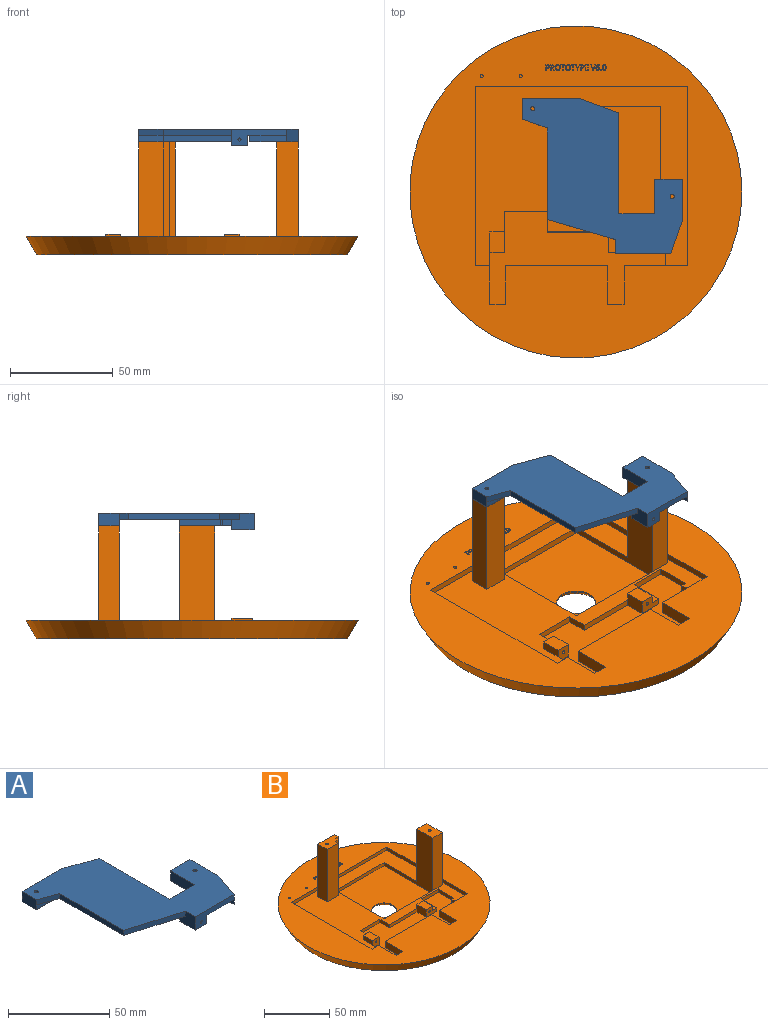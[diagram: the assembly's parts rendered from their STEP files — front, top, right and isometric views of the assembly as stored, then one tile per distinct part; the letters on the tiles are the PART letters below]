
ASSEMBLY  parts=2 mates=1
PART A: 32 faces, bbox 78x75.8x8 mm
  f0: plane 12x3mm, normal (0,-1,0), area 36mm2, adj f1,f5,f6,f20
  f1: plane 3x3mm, normal (1,0,0), area 9mm2, adj f0,f2,f6,f20
  f2: plane 35x3mm, normal (0,-1,0), area 105mm2, adj f1,f3,f6,f20
  f3: plane 19.23x7mm, normal (0.34,0.94,0), area 122.8mm2, adj f2,f4,f6,f21,f26
  f4: plane 27.77x6mm, normal (0,1,0), area 166.6mm2, adj f3,f5,f6,f26
  f5: plane 10x6mm, normal (-1,0,0), area 60mm2, adj f0,f4,f6,f22,f26
  f6: plane 47x10mm, normal (0,0,-1), area 294.5mm2, adj f0,f1,f2,f3,f4,f5,f31
  f7: plane 20x6mm, normal (1,0,0), area 120mm2, adj f8,f14,f15,f26
  f8: plane 13.5x6mm, normal (0,1,0), area 81mm2, adj f7,f9,f15,f26
  f9: plane 20x6mm, normal (-1,0,0), area 111mm2, adj f8,f10,f15,f20,f25,f26
  f10: plane 10.26x3mm, normal (0,1,0), area 30.8mm2, adj f9,f11,f15,f20
  f11: plane 3x1mm, normal (-1,0,0), area 3mm2, adj f10,f12,f15,f20
  f12: plane 18x3mm, normal (0,-1,0), area 54mm2, adj f11,f13,f15,f20
  f13: plane 15.5x3mm, normal (-1,0,0), area 46.5mm2, adj f12,f14,f15,f20
  f14: plane 16.5x6mm, normal (0.94,-0.33,0), area 104.9mm2, adj f7,f13,f15,f18,f26
  f15: plane 36.5x23.76mm, normal (0,0,-1), area 332.4mm2, adj f7,f8,f9,f10,f11,f12,f13,f14
  f16: plane 8x5mm, normal (0,1,0), area 40mm2, adj f17,f19,f20,f27
  f17: plane 11x8mm, normal (-1,0,0), area 76mm2, adj f16,f18,f20,f24,f26,f27
  f18: plane 27x8mm, normal (0,-1,0), area 119.2mm2, adj f14,f17,f19,f20,f26,f27,f28
  f19: plane 11x5mm, normal (1,0,0), area 55mm2, adj f16,f18,f20,f27
  f20: plane 72.24x68.8mm, normal (0,0,-1), area 2401.6mm2, adj f0,f1,f2,f9,f10,f11,f12,f13
  f21: plane 49.3x3mm, normal (1,0,0), area 147.9mm2, adj f3,f20,f25,f26
  f22: plane 12x4.37mm, normal (-0.34,-0.94,0), area 38.3mm2, adj f5,f20,f23,f26
  f23: plane 44.63x3mm, normal (-1,0,0), area 133.9mm2, adj f20,f22,f24,f26
  f24: plane 33.24x9.8mm, normal (-0.28,-0.96,0), area 104mm2, adj f17,f20,f23,f26
  f25: plane 17.5x3mm, normal (0,1,0), area 52.5mm2, adj f9,f20,f21,f26
  f26: plane 78x75.8mm, normal (0,0,1), area 3116.5mm2, adj f3,f4,f5,f7,f8,f9,f14,f17
  f27: plane 11x8mm, normal (0,0,-1), area 88mm2, adj f16,f17,f18,f19
  f28: cylinder r=0.75mm len=5mm, axis (0,-1,0), area 23.6mm2, adj f18,f29
  f29: plane 1.5x1.5mm, normal (0,-1,0), area 1.8mm2, adj f28
  f30: cylinder r=1mm len=6mm, axis (0,0,1), area 37.7mm2, adj f15,f26
  f31: cylinder r=1mm len=6mm, axis (0,0,1), area 37.7mm2, adj f6,f26
PART B: 260 faces, bbox 162x162x55 mm
  f0: plane 103.4x87.4mm, normal (0,0,1), area 4227.3mm2, adj f5,f6,f7,f8,f9,f16,f18,f19
  f1: plane 162x162mm, normal (0,0,1), area 11243.2mm2, adj f9,f10,f11,f12,f13,f14,f15,f16
  f2: plane 52.5x52.5mm, normal (0,0,1), area 2472.7mm2, adj f3,f24,f25,f26,f28
  f3: cylinder r=9.5mm len=19mm, axis (0,0,1), area 36.8mm2, adj f2,f41
  f4: plane 151.61x151.61mm, normal (0,0,-1), area 17636.8mm2, adj f40,f41
  f5: plane 18.5x3mm, normal (0,-1,0), area 55.5mm2, adj f0,f6,f27,f29
  f6: plane 17x3mm, normal (-1,0,0), area 51mm2, adj f0,f5,f7,f29
  f7: plane 3x2.5mm, normal (0,1,0), area 7.5mm2, adj f0,f6,f8,f29
  f8: plane 6.4x3mm, normal (-1,0,0), area 19.2mm2, adj f0,f7,f9,f29
  f9: plane 31x6mm, normal (0,1,0), area 153mm2, adj f0,f1,f8,f10,f29,f33
  f10: plane 19x6mm, normal (-1,0,0), area 114mm2, adj f1,f9,f11,f29
  f11: plane 8x6mm, normal (0,1,0), area 48mm2, adj f1,f10,f12,f29
  f12: plane 19x6mm, normal (1,0,0), area 114mm2, adj f1,f11,f13,f29
  f13: plane 50x6mm, normal (0,1,0), area 300mm2, adj f1,f12,f14,f29
  f14: plane 19x6mm, normal (-1,0,0), area 114mm2, adj f1,f13,f15,f29
  f15: plane 7.4x6mm, normal (0,1,0), area 44.4mm2, adj f1,f14,f16,f29
  f16: plane 25.4x6mm, normal (1,0,0), area 133.2mm2, adj f0,f1,f15,f17,f29,f30
  f17: plane 7x7mm, normal (0,-1,0), area 47.2mm2, adj f16,f18,f29,f35,f36,f44
  f18: plane 20x7mm, normal (1,0,0), area 100mm2, adj f0,f17,f19,f29,f34,f36
  f19: plane 21x3mm, normal (0,-1,0), area 63mm2, adj f0,f18,f20,f29
  f20: plane 10x3mm, normal (-1,0,0), area 30mm2, adj f0,f19,f21,f29
  f21: plane 29.9x3mm, normal (0,-1,0), area 89.7mm2, adj f0,f20,f22,f29
  f22: plane 10x7mm, normal (-1,0,0), area 70mm2, adj f21,f23,f29,f37,f39
  f23: plane 11.5x7mm, normal (0,-1,0), area 60.7mm2, adj f0,f22,f27,f29,f38,f39,f42
  f24: plane 52.5x52mm, normal (1,0,0), area 304.5mm2, adj f0,f2,f25,f28,f246,f251
  f25: plane 52.5x52mm, normal (0,-1,0), area 304.5mm2, adj f0,f2,f24,f26,f247,f251
  f26: plane 52.5x52mm, normal (-1,0,0), area 1000.3mm2, adj f0,f2,f25,f28,f253,f254,f255
  f27: plane 17x3mm, normal (1,0,0), area 51mm2, adj f0,f5,f23,f29
  f28: plane 52.5x3mm, normal (0,1,0), area 157.5mm2, adj f0,f2,f24,f26
  f29: plane 87.9x45.4mm, normal (0,0,1), area 1872.7mm2, adj f5,f6,f7,f8,f9,f10,f11,f12
  f30: plane 7x3mm, normal (0,1,0), area 21mm2, adj f0,f1,f16,f31
  f31: plane 87.4x3mm, normal (1,0,0), area 262.2mm2, adj f0,f1,f30,f32
  f32: plane 103.4x3mm, normal (0,-1,0), area 310.2mm2, adj f0,f1,f31,f33
  f33: plane 87.4x3mm, normal (-1,0,0), area 262.2mm2, adj f0,f1,f9,f32
  f34: plane 7x4mm, normal (0,1,0), area 28mm2, adj f0,f18,f35,f36
  f35: plane 10x4mm, normal (-1,0,0), area 40mm2, adj f0,f17,f34,f36
  f36: plane 10x7mm, normal (0,0,1), area 70mm2, adj f17,f18,f34,f35
  f37: plane 7x4mm, normal (0,1,0), area 28mm2, adj f0,f22,f38,f39
  f38: plane 10x4mm, normal (1,0,0), area 40mm2, adj f0,f23,f37,f39
  f39: plane 10x7mm, normal (0,0,1), area 70mm2, adj f22,f23,f37,f38
  f40: cone r=81mm half-angle=30deg, axis (0,0,1), area 5119.4mm2, adj f1,f4
  f41: cone r=11.5mm half-angle=40deg, axis (0,0,-1), area 205.3mm2, adj f3,f4
  f42: cylinder r=0.75mm len=5mm, axis (0,-1,0), area 23.6mm2, adj f23,f43
  f43: plane 1.5x1.5mm, normal (0,-1,0), area 1.8mm2, adj f42
  f44: cylinder r=0.75mm len=5mm, axis (0,-1,0), area 23.6mm2, adj f17,f45
  f45: plane 1.5x1.5mm, normal (0,-1,0), area 1.8mm2, adj f44
  f46: cylinder r=0.75mm len=3mm, axis (0,0,1), area 14.1mm2, adj f1,f47
  f47: plane 1.5x1.5mm, normal (0,0,1), area 1.8mm2, adj f46
  f48: cylinder r=0.75mm len=3mm, axis (0,0,1), area 14.1mm2, adj f1,f49
  f49: plane 1.5x1.5mm, normal (0,0,1), area 1.8mm2, adj f48
  f50: plane 0.5x0.32mm, normal (0,1,0), area 0.2mm2, adj f1,f51,f57,f58
  f51: plane 2.44x0.5mm, normal (-1,0,0), area 1.2mm2, adj f1,f50,f52,f58
  f52: plane 0.86x0.5mm, normal (0,1,0), area 0.4mm2, adj f1,f51,f53,f58
  f53: plane 0.5x0.28mm, normal (-1,0,0), area 0.1mm2, adj f1,f52,f54,f58
  f54: plane 2.04x0.5mm, normal (0,-1,0), area 1mm2, adj f1,f53,f55,f58
  f55: plane 0.5x0.28mm, normal (1,0,0), area 0.1mm2, adj f1,f54,f56,f58
  f56: plane 0.86x0.5mm, normal (0,1,0), area 0.4mm2, adj f1,f55,f57,f58
  f57: plane 2.44x0.5mm, normal (1,0,0), area 1.2mm2, adj f1,f50,f56,f58
  f58: plane 2.72x2.04mm, normal (0,0,1), area 1.3mm2, adj f50,f51,f52,f53,f54,f55,f56,f57
  f59: extruded ~0.86x0.5mm, area 0.4mm2, adj f60,f74,f75,f238
  f60: extruded ~0.86x0.5mm, area 0.4mm2, adj f59,f61,f75,f238
  f61: extruded ~0.5x0.44mm, area 0.3mm2, adj f60,f62,f75,f238
  f62: extruded ~0.5x0.45mm, area 0.3mm2, adj f61,f63,f75,f238
  f63: extruded ~0.86x0.5mm, area 0.4mm2, adj f62,f64,f75,f238
  f64: extruded ~0.86x0.5mm, area 0.4mm2, adj f63,f65,f75,f238
  f65: extruded ~0.5x0.45mm, area 0.3mm2, adj f64,f74,f75,f238
  f66: extruded ~1.05x0.5mm, area 0.5mm2, adj f1,f67,f73,f75
  f67: extruded ~1.04x0.5mm, area 0.5mm2, adj f1,f66,f68,f75
  f68: extruded ~0.67x0.5mm, area 0.4mm2, adj f1,f67,f69,f75
  f69: extruded ~0.67x0.5mm, area 0.4mm2, adj f1,f68,f70,f75
  f70: extruded ~1.05x0.5mm, area 0.5mm2, adj f1,f69,f71,f75
  f71: extruded ~1.04x0.5mm, area 0.5mm2, adj f1,f70,f72,f75
  f72: extruded ~0.67x0.5mm, area 0.4mm2, adj f1,f71,f73,f75
  f73: extruded ~0.68x0.5mm, area 0.4mm2, adj f1,f66,f72,f75
  f74: extruded ~0.5x0.44mm, area 0.3mm2, adj f59,f65,f75,f238
  f75: plane 2.8x1.8mm, normal (0,0,1), area 1.9mm2, adj f59,f60,f61,f62,f63,f64,f65,f66
  f76: extruded ~0.5x0.41mm, area 0.2mm2, adj f77,f100,f101,f239
  f77: extruded ~0.5x0.31mm, area 0.2mm2, adj f76,f78,f101,f239
  f78: extruded ~0.5x0.26mm, area 0.2mm2, adj f77,f79,f101,f239
  f79: extruded ~0.5x0.36mm, area 0.2mm2, adj f78,f80,f101,f239
  f80: extruded ~0.5x0.25mm, area 0.1mm2, adj f79,f81,f101,f239
  f81: extruded ~0.5x0.22mm, area 0.1mm2, adj f80,f82,f101,f239
  f82: extruded ~0.5x0.31mm, area 0.2mm2, adj f81,f83,f101,f239
  f83: extruded ~0.5x0.41mm, area 0.2mm2, adj f82,f84,f101,f239
  f84: extruded ~0.5x0.42mm, area 0.2mm2, adj f83,f100,f101,f239
  f85: extruded ~1.2x0.5mm, area 0.6mm2, adj f1,f86,f99,f101
  f86: extruded ~0.88x0.5mm, area 0.5mm2, adj f1,f85,f87,f101
  f87: extruded ~0.67x0.5mm, area 0.4mm2, adj f1,f86,f88,f101
  f88: extruded ~0.63x0.5mm, area 0.3mm2, adj f1,f87,f89,f101
  f89: extruded ~0.67x0.5mm, area 0.4mm2, adj f1,f88,f90,f101
  f90: extruded ~0.6x0.5mm, area 0.3mm2, adj f1,f89,f91,f101
  f91: extruded ~0.58x0.5mm, area 0.3mm2, adj f1,f90,f92,f101
  f92: extruded ~0.65x0.5mm, area 0.4mm2, adj f1,f91,f93,f101
  f93: plane 0.5x0.02mm, normal (0,-1,0), area 0mm2, adj f1,f92,f94,f101
  f94: extruded ~0.86x0.5mm, area 0.5mm2, adj f1,f93,f95,f101
  f95: extruded ~0.67x0.5mm, area 0.4mm2, adj f1,f94,f96,f101
  f96: extruded ~0.5x0.33mm, area 0.2mm2, adj f1,f95,f97,f101
  f97: plane 0.5x0.27mm, normal (-1,0,0), area 0.1mm2, adj f1,f96,f98,f101
  f98: extruded ~0.5x0.33mm, area 0.2mm2, adj f1,f97,f99,f101
  f99: extruded ~0.92x0.5mm, area 0.5mm2, adj f1,f85,f98,f101
  f100: extruded ~0.5x0.48mm, area 0.3mm2, adj f76,f84,f101,f239
  f101: plane 2.79x1.77mm, normal (0,0,1), area 1.9mm2, adj f76,f77,f78,f79,f80,f81,f82,f83
  f102: plane 0.5x0.29mm, normal (0,-1,0), area 0.1mm2, adj f103,f116,f117,f240
  f103: plane 1.1x0.5mm, normal (-1,0,0), area 0.6mm2, adj f102,f104,f117,f240
  f104: plane 0.5x0.35mm, normal (0,1,0), area 0.2mm2, adj f103,f105,f117,f240
  f105: extruded ~0.55x0.5mm, area 0.3mm2, adj f104,f106,f117,f240
  f106: extruded ~0.5x0.4mm, area 0.2mm2, adj f105,f107,f117,f240
  f107: extruded ~0.5x0.44mm, area 0.2mm2, adj f106,f116,f117,f240
  f108: extruded ~0.64x0.5mm, area 0.4mm2, adj f1,f109,f115,f117
  f109: extruded ~1.02x0.79mm, area 0.7mm2, adj f1,f108,f110,f117
  f110: plane 0.7x0.5mm, normal (0,-1,0), area 0.4mm2, adj f1,f109,f111,f117
  f111: plane 2.72x0.5mm, normal (1,0,0), area 1.4mm2, adj f1,f110,f112,f117
  f112: plane 0.5x0.32mm, normal (0,1,0), area 0.2mm2, adj f1,f111,f113,f117
  f113: plane 1.07x0.5mm, normal (-1,0,0), area 0.5mm2, adj f1,f112,f114,f117
  f114: plane 0.5x0.32mm, normal (0,1,0), area 0.2mm2, adj f1,f113,f115,f117
  f115: extruded ~0.81x0.5mm, area 0.4mm2, adj f1,f108,f114,f117
  f116: extruded ~0.61x0.5mm, area 0.3mm2, adj f102,f107,f117,f240
  f117: plane 2.72x1.72mm, normal (0,0,1), area 1.8mm2, adj f102,f103,f104,f105,f106,f107,f108,f109
  f118: extruded ~0.84x0.5mm, area 0.4mm2, adj f119,f133,f134,f241
  f119: extruded ~0.83x0.5mm, area 0.4mm2, adj f118,f120,f134,f241
  f120: extruded ~0.69x0.5mm, area 0.4mm2, adj f119,f121,f134,f241
  f121: extruded ~0.68x0.5mm, area 0.4mm2, adj f120,f122,f134,f241
  f122: extruded ~0.83x0.5mm, area 0.4mm2, adj f121,f123,f134,f241
  f123: extruded ~0.84x0.5mm, area 0.4mm2, adj f122,f124,f134,f241
  f124: extruded ~0.68x0.5mm, area 0.4mm2, adj f123,f133,f134,f241
  f125: extruded ~1.03x0.5mm, area 0.6mm2, adj f1,f126,f132,f134
  f126: extruded ~1.03x0.5mm, area 0.6mm2, adj f1,f125,f127,f134
  f127: extruded ~0.91x0.5mm, area 0.5mm2, adj f1,f126,f128,f134
  f128: extruded ~0.93x0.5mm, area 0.5mm2, adj f1,f127,f129,f134
  f129: extruded ~1.03x0.5mm, area 0.6mm2, adj f1,f128,f130,f134
  f130: extruded ~1.04x0.5mm, area 0.6mm2, adj f1,f129,f131,f134
  f131: extruded ~0.93x0.5mm, area 0.5mm2, adj f1,f130,f132,f134
  f132: extruded ~0.92x0.5mm, area 0.5mm2, adj f1,f125,f131,f134
  f133: extruded ~0.68x0.5mm, area 0.4mm2, adj f118,f124,f134,f241
  f134: plane 2.8x2.5mm, normal (0,0,1), area 2.3mm2, adj f118,f119,f120,f121,f122,f123,f124,f125
  f135: plane 0.5x0.32mm, normal (0,1,0), area 0.2mm2, adj f1,f136,f142,f143
  f136: plane 2.44x0.5mm, normal (-1,0,0), area 1.2mm2, adj f1,f135,f137,f143
  f137: plane 0.86x0.5mm, normal (0,1,0), area 0.4mm2, adj f1,f136,f138,f143
  f138: plane 0.5x0.28mm, normal (-1,0,0), area 0.1mm2, adj f1,f137,f139,f143
  f139: plane 2.04x0.5mm, normal (0,-1,0), area 1mm2, adj f1,f138,f140,f143
  f140: plane 0.5x0.28mm, normal (1,0,0), area 0.1mm2, adj f1,f139,f141,f143
  f141: plane 0.86x0.5mm, normal (0,1,0), area 0.4mm2, adj f1,f140,f142,f143
  f142: plane 2.44x0.5mm, normal (1,0,0), area 1.2mm2, adj f1,f135,f141,f143
  f143: plane 2.72x2.04mm, normal (0,0,1), area 1.3mm2, adj f135,f136,f137,f138,f139,f140,f141,f142
  f144: plane 1.36x0.72mm, normal (0.88,-0.47,0), area 0.8mm2, adj f1,f145,f152,f153
  f145: plane 1.36x0.72mm, normal (-0.88,-0.47,0), area 0.8mm2, adj f1,f144,f146,f153
  f146: plane 0.5x0.35mm, normal (0,-1,0), area 0.2mm2, adj f1,f145,f147,f153
  f147: plane 1.68x0.91mm, normal (0.88,0.47,0), area 1mm2, adj f1,f146,f148,f153
  f148: plane 1.04x0.5mm, normal (1,0,0), area 0.5mm2, adj f1,f147,f149,f153
  f149: plane 0.5x0.32mm, normal (0,1,0), area 0.2mm2, adj f1,f148,f150,f153
  f150: plane 1.05x0.5mm, normal (-1,0,0), area 0.5mm2, adj f1,f149,f151,f153
  f151: plane 1.66x0.91mm, normal (-0.88,0.48,0), area 0.9mm2, adj f1,f150,f152,f153
  f152: plane 0.5x0.34mm, normal (0,-1,0), area 0.2mm2, adj f1,f144,f151,f153
  f153: plane 2.72x2.13mm, normal (0,0,1), area 1.4mm2, adj f144,f145,f146,f147,f148,f149,f150,f151
  f154: plane 1.51x0.5mm, normal (0,1,0), area 0.8mm2, adj f1,f155,f165,f166
  f155: plane 0.5x0.28mm, normal (-1,0,0), area 0.1mm2, adj f1,f154,f156,f166
  f156: plane 1.2x0.5mm, normal (0,-1,0), area 0.6mm2, adj f1,f155,f157,f166
  f157: plane 1x0.5mm, normal (-1,0,0), area 0.5mm2, adj f1,f156,f158,f166
  f158: plane 1.13x0.5mm, normal (0,1,0), area 0.6mm2, adj f1,f157,f159,f166
  f159: plane 0.5x0.28mm, normal (-1,0,0), area 0.1mm2, adj f1,f158,f160,f166
  f160: plane 1.13x0.5mm, normal (0,-1,0), area 0.6mm2, adj f1,f159,f161,f166
  f161: plane 0.88x0.5mm, normal (-1,0,0), area 0.4mm2, adj f1,f160,f162,f166
  f162: plane 1.2x0.5mm, normal (0,1,0), area 0.6mm2, adj f1,f161,f163,f166
  f163: plane 0.5x0.28mm, normal (-1,0,0), area 0.1mm2, adj f1,f162,f164,f166
  f164: plane 1.51x0.5mm, normal (0,-1,0), area 0.8mm2, adj f1,f163,f165,f166
  f165: plane 2.72x0.5mm, normal (1,0,0), area 1.4mm2, adj f1,f154,f164,f166
  f166: plane 2.72x1.51mm, normal (0,0,1), area 1.8mm2, adj f154,f155,f156,f157,f158,f159,f160,f161
  f167: plane 0.5x0.34mm, normal (0,-1,0), area 0.2mm2, adj f1,f168,f175,f176
  f168: plane 1.75x0.62mm, normal (0.94,-0.33,0), area 0.9mm2, adj f1,f167,f169,f176
  f169: extruded ~0.6x0.5mm, area 0.3mm2, adj f1,f168,f170,f176
  f170: extruded ~0.59x0.5mm, area 0.3mm2, adj f1,f169,f171,f176
  f171: plane 1.76x0.62mm, normal (-0.94,-0.33,0), area 0.9mm2, adj f1,f170,f172,f176
  f172: plane 0.5x0.34mm, normal (0,-1,0), area 0.2mm2, adj f1,f171,f173,f176
  f173: plane 2.72x0.97mm, normal (0.94,0.34,0), area 1.4mm2, adj f1,f172,f174,f176
  f174: plane 0.5x0.31mm, normal (0,1,0), area 0.2mm2, adj f1,f173,f175,f176
  f175: plane 2.72x0.98mm, normal (-0.94,0.34,0), area 1.4mm2, adj f1,f167,f174,f176
  f176: plane 2.72x2.27mm, normal (0,0,1), area 1.7mm2, adj f167,f168,f169,f170,f171,f172,f173,f174
  f177: extruded ~0.84x0.5mm, area 0.4mm2, adj f178,f192,f193,f242
  f178: extruded ~0.83x0.5mm, area 0.4mm2, adj f177,f179,f193,f242
  f179: extruded ~0.69x0.5mm, area 0.4mm2, adj f178,f180,f193,f242
  f180: extruded ~0.68x0.5mm, area 0.4mm2, adj f179,f181,f193,f242
  f181: extruded ~0.83x0.5mm, area 0.4mm2, adj f180,f182,f193,f242
  f182: extruded ~0.84x0.5mm, area 0.4mm2, adj f181,f183,f193,f242
  f183: extruded ~0.68x0.5mm, area 0.4mm2, adj f182,f192,f193,f242
  f184: extruded ~1.03x0.5mm, area 0.6mm2, adj f1,f185,f191,f193
  f185: extruded ~1.03x0.5mm, area 0.6mm2, adj f1,f184,f186,f193
  f186: extruded ~0.91x0.5mm, area 0.5mm2, adj f1,f185,f187,f193
  f187: extruded ~0.93x0.5mm, area 0.5mm2, adj f1,f186,f188,f193
  f188: extruded ~1.03x0.5mm, area 0.6mm2, adj f1,f187,f189,f193
  f189: extruded ~1.04x0.5mm, area 0.6mm2, adj f1,f188,f190,f193
  f190: extruded ~0.93x0.5mm, area 0.5mm2, adj f1,f189,f191,f193
  f191: extruded ~0.92x0.5mm, area 0.5mm2, adj f1,f184,f190,f193
  f192: extruded ~0.68x0.5mm, area 0.4mm2, adj f177,f183,f193,f242
  f193: plane 2.8x2.5mm, normal (0,0,1), area 2.3mm2, adj f177,f178,f179,f180,f181,f182,f183,f184
  f194: plane 0.5x0.43mm, normal (0,-1,0), area 0.2mm2, adj f195,f211,f212,f243
  f195: plane 1.04x0.5mm, normal (-1,0,0), area 0.5mm2, adj f194,f196,f212,f243
  f196: plane 0.5x0.41mm, normal (0,1,0), area 0.2mm2, adj f195,f197,f212,f243
  f197: extruded ~0.51x0.5mm, area 0.3mm2, adj f196,f198,f212,f243
  f198: extruded ~0.5x0.39mm, area 0.2mm2, adj f197,f199,f212,f243
  f199: extruded ~0.5x0.4mm, area 0.2mm2, adj f198,f211,f212,f243
  f200: plane 1.13x0.5mm, normal (-1,0,0), area 0.6mm2, adj f1,f201,f210,f212
  f201: plane 0.57x0.5mm, normal (0,1,0), area 0.3mm2, adj f1,f200,f202,f212
  f202: plane 1.13x0.66mm, normal (0.86,0.5,0), area 0.7mm2, adj f1,f201,f203,f212
  f203: plane 0.5x0.37mm, normal (0,1,0), area 0.2mm2, adj f1,f202,f204,f212
  f204: plane 1.22x0.74mm, normal (-0.86,-0.52,0), area 0.7mm2, adj f1,f203,f205,f212
  f205: extruded ~0.73x0.55mm, area 0.5mm2, adj f1,f204,f206,f212
  f206: extruded ~0.58x0.5mm, area 0.3mm2, adj f1,f205,f207,f212
  f207: extruded ~0.74x0.5mm, area 0.4mm2, adj f1,f206,f208,f212
  f208: plane 0.75x0.5mm, normal (0,-1,0), area 0.4mm2, adj f1,f207,f209,f212
  f209: plane 2.72x0.5mm, normal (1,0,0), area 1.4mm2, adj f1,f208,f210,f212
  f210: plane 0.5x0.32mm, normal (0,1,0), area 0.2mm2, adj f1,f200,f209,f212
  f211: extruded ~0.5x0.49mm, area 0.3mm2, adj f194,f199,f212,f243
  f212: plane 2.72x1.91mm, normal (0,0,1), area 2.2mm2, adj f194,f195,f196,f197,f198,f199,f200,f201
  f213: plane 0.5x0.29mm, normal (0,-1,0), area 0.1mm2, adj f214,f227,f228,f244
  f214: plane 1.1x0.5mm, normal (-1,0,0), area 0.6mm2, adj f213,f215,f228,f244
  f215: plane 0.5x0.35mm, normal (0,1,0), area 0.2mm2, adj f214,f216,f228,f244
  f216: extruded ~0.55x0.5mm, area 0.3mm2, adj f215,f217,f228,f244
  f217: extruded ~0.5x0.4mm, area 0.2mm2, adj f216,f218,f228,f244
  f218: extruded ~0.5x0.44mm, area 0.2mm2, adj f217,f227,f228,f244
  f219: extruded ~0.64x0.5mm, area 0.4mm2, adj f1,f220,f226,f228
  f220: extruded ~1.02x0.79mm, area 0.7mm2, adj f1,f219,f221,f228
  f221: plane 0.7x0.5mm, normal (0,-1,0), area 0.4mm2, adj f1,f220,f222,f228
  f222: plane 2.72x0.5mm, normal (1,0,0), area 1.4mm2, adj f1,f221,f223,f228
  f223: plane 0.5x0.32mm, normal (0,1,0), area 0.2mm2, adj f1,f222,f224,f228
  f224: plane 1.07x0.5mm, normal (-1,0,0), area 0.5mm2, adj f1,f223,f225,f228
  f225: plane 0.5x0.32mm, normal (0,1,0), area 0.2mm2, adj f1,f224,f226,f228
  f226: extruded ~0.81x0.5mm, area 0.4mm2, adj f1,f219,f225,f228
  f227: extruded ~0.61x0.5mm, area 0.3mm2, adj f213,f218,f228,f244
  f228: plane 2.72x1.72mm, normal (0,0,1), area 1.8mm2, adj f213,f214,f215,f216,f217,f218,f219,f220
  f229: extruded ~0.5x0.19mm, area 0.1mm2, adj f1,f230,f236,f237
  f230: extruded ~0.5x0.19mm, area 0.1mm2, adj f1,f229,f231,f237
  f231: extruded ~0.5x0.16mm, area 0.1mm2, adj f1,f230,f232,f237
  f232: extruded ~0.5x0.17mm, area 0.1mm2, adj f1,f231,f233,f237
  f233: extruded ~0.5x0.19mm, area 0.1mm2, adj f1,f232,f234,f237
  f234: extruded ~0.5x0.19mm, area 0.1mm2, adj f1,f233,f235,f237
  f235: extruded ~0.5x0.17mm, area 0.1mm2, adj f1,f234,f236,f237
  f236: extruded ~0.5x0.16mm, area 0.1mm2, adj f1,f229,f235,f237
  f237: plane 0.5x0.45mm, normal (0,0,1), area 0.2mm2, adj f229,f230,f231,f232,f233,f234,f235,f236
  f238: plane 2.26x1.17mm, normal (0,0,1), area 2.2mm2, adj f59,f60,f61,f62,f63,f64,f65,f74
  f239: plane 1.23x1.15mm, normal (0,0,1), area 1.1mm2, adj f76,f77,f78,f79,f80,f81,f82,f83
  f240: plane 1.1x1.08mm, normal (0,0,1), area 1.1mm2, adj f102,f103,f104,f105,f106,f107,f116
  f241: plane 2.24x1.83mm, normal (0,0,1), area 3.4mm2, adj f118,f119,f120,f121,f122,f123,f124,f133
  f242: plane 2.24x1.83mm, normal (0,0,1), area 3.4mm2, adj f177,f178,f179,f180,f181,f182,f183,f192
  f243: plane 1.08x1.04mm, normal (0,0,1), area 1mm2, adj f194,f195,f196,f197,f198,f199,f211
  f244: plane 1.1x1.08mm, normal (0,0,1), area 1.1mm2, adj f213,f214,f215,f216,f217,f218,f227
  f245: plane 49x3mm, normal (1,0,0), area 147mm2, adj f0,f246,f250,f251
  f246: plane 49x3mm, normal (0,-1,0), area 147mm2, adj f0,f24,f245,f251
  f247: plane 49x4mm, normal (1,0,0), area 196mm2, adj f0,f25,f248,f251
  f248: plane 49x18mm, normal (0,1,0), area 882mm2, adj f0,f247,f249,f251
  f249: plane 49x10mm, normal (-1,0,0), area 490mm2, adj f0,f248,f250,f251
  f250: plane 49x12mm, normal (0,-1,0), area 588mm2, adj f0,f245,f249,f251
  f251: plane 18x10mm, normal (0,0,1), area 149.9mm2, adj f24,f25,f245,f246,f247,f248,f249,f250
  f252: plane 49x17.2mm, normal (1,0,0), area 842.8mm2, adj f0,f253,f254,f255
  f253: plane 49x10.5mm, normal (0,1,0), area 514.5mm2, adj f0,f26,f252,f255
  f254: plane 49x10.5mm, normal (0,-1,0), area 514.5mm2, adj f0,f26,f252,f255
  f255: plane 17.2x10.5mm, normal (0,0,1), area 177.5mm2, adj f26,f252,f253,f254,f258
  f256: cylinder r=1mm len=5mm, axis (0,0,1), area 31.4mm2, adj f251,f257
  f257: plane 2x2mm, normal (0,0,1), area 3.1mm2, adj f256
  f258: cylinder r=1mm len=5mm, axis (0,0,1), area 31.4mm2, adj f255,f259
  f259: plane 2x2mm, normal (0,0,1), area 3.1mm2, adj f258
PLACE A t=(-13.9,-3.89,59.7)mm
PLACE B t=(-13.9,-4.09,4.5)mm
MATE parallel A.f6 <-> B.f251  axis (0,0,1) through (-12.14,41.41,56.7)mm
